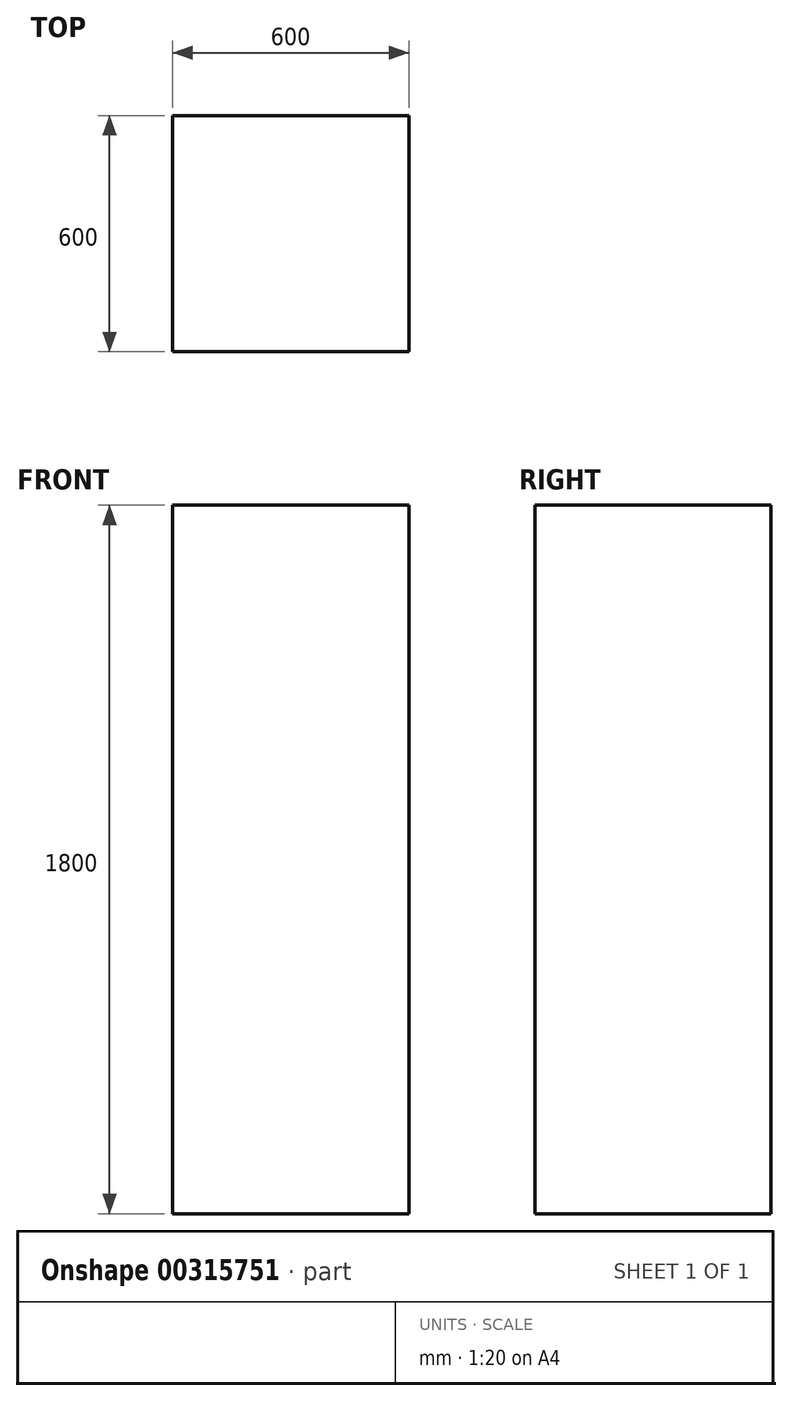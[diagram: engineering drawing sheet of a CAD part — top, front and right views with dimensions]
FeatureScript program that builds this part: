
annotation { "Feature Type Name" : "Feature", "Feature Type Description" : "" }
export const myFeature = defineFeature(function(context is Context, id is Id, definition is map)
    precondition{}
    {
        {
            var Q0;
            Q0=qCreatedBy(makeId("Top.planeOp"),FACE);
            var sketch = newSketch(context, id + "F0", { "sketchPlane" : qUnion([Q0])});
            skLineSegment(sketch, "E0.bottom", {"start": v(-109.21, 463.79) * mm, "end": v(490.79, 463.79) * mm});
            skLineSegment(sketch, "E0.top", {"start": v(-109.21, -136.21) * mm, "end": v(490.79, -136.21) * mm});
            skLineSegment(sketch, "E0.left", {"start": v(-109.21, 463.79) * mm, "end": v(-109.21, -136.21) * mm});
            skLineSegment(sketch, "E0.right", {"start": v(490.79, 463.79) * mm, "end": v(490.79, -136.21) * mm});
            skSolve(sketch);
        }
        {
            var Q0;
            Q0=makeQuery(id+"F0.imprint","IMPRINT",FACE,{"disambiguationData":[TD([[makeQuery(id+"F0.imprint","IMPRINT",EDGE,{"derivedFrom":sQuery(id+"F0.wireOp",EDGE,"E0.bottom")}),-1.0]])]});
            extrude(context, id + "F1", {"entities" : qUnion([Q0]), "depth" : 1800 * mm});
        }
    });
